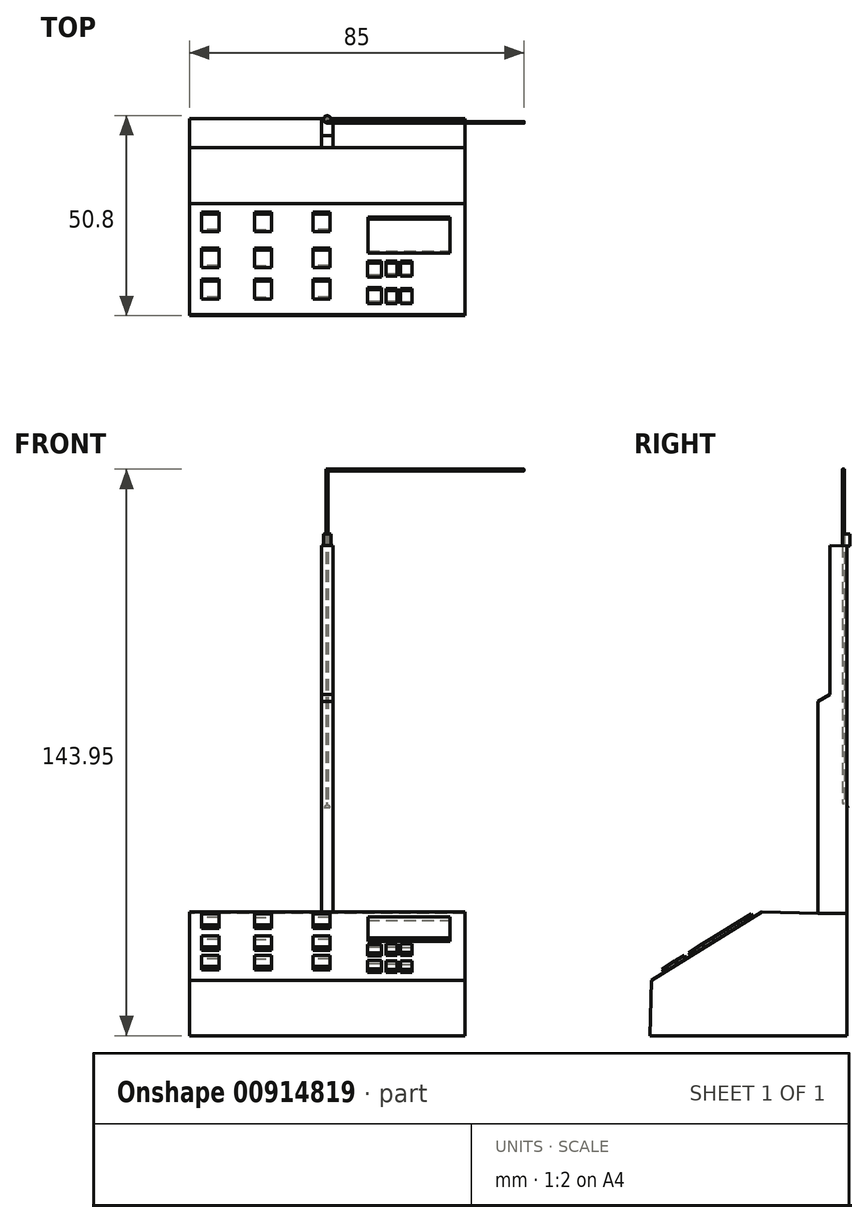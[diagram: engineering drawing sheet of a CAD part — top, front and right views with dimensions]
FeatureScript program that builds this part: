
annotation { "Feature Type Name" : "Feature", "Feature Type Description" : "" }
export const myFeature = defineFeature(function(context is Context, id is Id, definition is map)
    precondition{}
    {
        {
            var Q0;
            Q0=qCreatedBy(makeId("Right.planeOp"),FACE);
            var sketch = newSketch(context, id + "F0", { "sketchPlane" : qUnion([Q0])});
            skLineSegment(sketch, "E0", {"start": v(0, 124.44) * mm, "end": v(0, 0) * mm});
            skLineSegment(sketch, "E1", {"start": v(0, 0) * mm, "end": v(-50, 0) * mm});
            skLineSegment(sketch, "E2", {"start": v(-50, 0) * mm, "end": v(-49.7, 14.02) * mm});
            skLineSegment(sketch, "E3", {"start": v(-49.7, 14.02) * mm, "end": v(-21.55, 31.4) * mm});
            skLineSegment(sketch, "E4", {"start": v(-21.55, 31.4) * mm, "end": v(-7.35, 31.1) * mm});
            skLineSegment(sketch, "E5", {"start": v(-7.35, 31.1) * mm, "end": v(-7.35, 84.93) * mm});
            skLineSegment(sketch, "E6", {"start": v(-7.35, 84.93) * mm, "end": v(-4.25, 86.74) * mm});
            skLineSegment(sketch, "E7", {"start": v(-4.25, 86.74) * mm, "end": v(-4.25, 124.49) * mm});
            skLineSegment(sketch, "E8", {"start": v(-4.25, 124.49) * mm, "end": v(0, 124.44) * mm});
            skLineSegment(sketch, "E9", {"start": v(-7.35, 31.1) * mm, "end": v(0, 31.1) * mm});
            skSolve(sketch);
        }
        {
            var Q0;
            {var subQ0=sQuery(id+"F0.wireOp",EDGE,"E1");Q0=makeQuery(id+"F0.imprint","IMPRINT",FACE,{"disambiguationData":[TD([[makeQuery(id+"F0.imprint","IMPRINT",EDGE,{"derivedFrom":subQ0}),-1.0]])]});}
            extrude(context, id + "F1", {"entities" : qUnion([Q0]), "endBound" : BoundingType.SYMMETRIC, "depth" : 70 * mm, "offsetDistance" : 25 * mm});
        }
        {
            var Q0;
            Q0 = qSketchRegion(id + "F0", true);
            extrude(context, id + "F2", {"entities" : qUnion([Q0]), "operationType" : NewBodyOperationType.ADD, "endBound" : BoundingType.SYMMETRIC, "depth" : 3 * mm, "offsetDistance" : 25 * mm});
        }
        {
            var Q0;
            Q0=makeQuery(id+"F2.opExtrude","SWEPT_FACE",FACE,{"disambiguationData":[OSD([sQuery(id+"F0.wireOp",EDGE,"E8")])]});
            var sketch = newSketch(context, id + "F3", { "sketchPlane" : qUnion([Q0])});
            skCircle(sketch, "E10", {"center": v(0, -1.6) * mm, "radius": 0.9 * mm});
            skSolve(sketch);
        }
        {
            var Q0;
            Q0 = qSketchRegion(id + "F3", true);
            extrude(context, id + "F4", {"entities" : qUnion([Q0]), "operationType" : NewBodyOperationType.ADD, "depth" : 3 * mm, "offsetDistance" : 25 * mm});
        }
        {
            var Q0;
            Q0=qCreatedBy(makeId("Front.planeOp"),FACE);
            cPlane(context, id + "F5", {"entities" : qUnion([Q0]), "cplaneType" : CPlaneType.OFFSET, "offset" : 0.9 * mm, "width" : 150 * mm, "height" : 150 * mm});
        }
        {
            var Q0;
            Q0=qCreatedBy(id+"F5.planeOp",FACE);
            var sketch = newSketch(context, id + "F6", { "sketchPlane" : qUnion([Q0])});
            skLineSegment(sketch, "E11", {"start": v(0, 57.63) * mm, "end": v(0, 58.95) * mm});
            skArc(sketch, "E12", {"start": v(0, 58.95) * mm, "mid": v(-0.77, 58.67) * mm, "end": v(-1.18, 57.97) * mm});
            skLineSegment(sketch, "E13", {"start": v(-0.9, 57.97) * mm, "end": v(-1.18, 57.97) * mm});
            skLineSegment(sketch, "E14", {"start": v(-1.18, 57.97) * mm, "end": v(0, 57.97) * mm});
            skSolve(sketch);
        }
        {
            var Q0;
            Q0 = qSketchRegion(id + "F6", true);
            var Q1;
            Q1=sQuery(id+"F6.wireOp",EDGE,"E11");
            revolve(context, id + "F7", {"operationType" : NewBodyOperationType.ADD, "surfaceOperationType" : NewSurfaceOperationType.NEW, "entities" : qUnion([Q0]), "axis" : qUnion([Q1]), "revolveType" : RevolveType.FULL});
        }
        {
            var Q0;
            Q0=qCreatedBy(makeId("Top.planeOp"),FACE);
            cPlane(context, id + "F8", {"entities" : qUnion([Q0]), "cplaneType" : CPlaneType.OFFSET, "offset" : 58.95 * mm, "width" : 150 * mm, "height" : 150 * mm});
        }
        {
            var Q0;
            Q0=qCreatedBy(id+"F8.planeOp",FACE);
            var sketch = newSketch(context, id + "F9", { "sketchPlane" : qUnion([Q0])});
            skCircle(sketch, "E15", {"center": v(0, -0.9) * mm, "radius": 0.25 * mm});
            skSolve(sketch);
        }
        {
            var Q0;
            Q0 = qSketchRegion(id + "F9", true);
            extrude(context, id + "F10", {"entities" : qUnion([Q0]), "depth" : 85 * mm, "offsetDistance" : 25 * mm});
        }
        {
            var Q0;
            Q0=qCreatedBy(makeId("Right.planeOp"),FACE);
            var sketch = newSketch(context, id + "F11", { "sketchPlane" : qUnion([Q0])});
            skCircle(sketch, "E16", {"center": v(-0.9, 143.72) * mm, "radius": 0.22 * mm});
            skSolve(sketch);
        }
        {
            var Q0;
            Q0 = qSketchRegion(id + "F11", true);
            extrude(context, id + "F12", {"entities" : qUnion([Q0]), "operationType" : NewBodyOperationType.ADD, "depth" : 50 * mm, "offsetDistance" : 25 * mm});
        }
        {
            var Q0;
            Q0=makeQuery(id+"F1.opExtrude","SWEPT_FACE",FACE,{"disambiguationData":[OSD([sQuery(id+"F0.wireOp",EDGE,"E3")])]});
            var sketch = newSketch(context, id + "F13", { "sketchPlane" : qUnion([Q0])});
            skLineSegment(sketch, "E17.bottom", {"start": v(-27.54, -9.63) * mm, "end": v(-31.88, -9.63) * mm});
            skLineSegment(sketch, "E17.top", {"start": v(-27.54, -4.3) * mm, "end": v(-31.88, -4.3) * mm});
            skLineSegment(sketch, "E17.left", {"start": v(-27.54, -9.63) * mm, "end": v(-27.54, -4.3) * mm});
            skLineSegment(sketch, "E17.right", {"start": v(-31.88, -9.63) * mm, "end": v(-31.88, -4.3) * mm});
            skPoint(sketch, "E17.middle", {"position": v(-29.71, -6.96) * mm});
            skLineSegment(sketch, "E18", {"start": v(-23.03, -3.38) * mm, "end": v(-23.03, -27.56) * mm});
            skLineSegment(sketch, "E19", {"start": v(-8.92, -3.02) * mm, "end": v(-8.92, -27.82) * mm});
            skLineSegment(sketch, "E20", {"start": v(-32.63, -22.37) * mm, "end": v(1.6, -22.37) * mm});
            skLineSegment(sketch, "E21.MirrorCS", {"start": v(-18.52, -4.3) * mm, "end": v(-14.18, -4.3) * mm});
            skLineSegment(sketch, "E22.MirrorCS", {"start": v(-18.52, -9.63) * mm, "end": v(-18.52, -4.3) * mm});
            skLineSegment(sketch, "E23.MirrorCS", {"start": v(-18.52, -9.63) * mm, "end": v(-14.18, -9.63) * mm});
            skLineSegment(sketch, "E24.MirrorCS", {"start": v(-14.18, -9.63) * mm, "end": v(-14.18, -4.3) * mm});
            skLineSegment(sketch, "E25.MirrorCS", {"start": v(-27.54, -15.05) * mm, "end": v(-27.54, -20.37) * mm});
            skLineSegment(sketch, "E26.MirrorCS", {"start": v(-27.54, -20.37) * mm, "end": v(-31.88, -20.37) * mm});
            skLineSegment(sketch, "E27.MirrorCS", {"start": v(-31.88, -15.05) * mm, "end": v(-31.88, -20.37) * mm});
            skLineSegment(sketch, "E28.MirrorCS", {"start": v(-27.54, -15.05) * mm, "end": v(-31.88, -15.05) * mm});
            skLineSegment(sketch, "E29.MirrorCS", {"start": v(-18.52, -15.05) * mm, "end": v(-14.18, -15.05) * mm});
            skLineSegment(sketch, "E30.MirrorCS", {"start": v(-18.52, -15.05) * mm, "end": v(-18.52, -20.37) * mm});
            skLineSegment(sketch, "E31.MirrorCS", {"start": v(-18.52, -20.37) * mm, "end": v(-14.18, -20.37) * mm});
            skLineSegment(sketch, "E32.MirrorCS", {"start": v(-14.18, -15.05) * mm, "end": v(-14.18, -20.37) * mm});
            skLineSegment(sketch, "E33.MirrorCS", {"start": v(-3.67, -9.63) * mm, "end": v(-3.67, -4.3) * mm});
            skLineSegment(sketch, "E34.MirrorCS", {"start": v(0.68, -9.63) * mm, "end": v(-3.67, -9.63) * mm});
            skLineSegment(sketch, "E35.MirrorCS", {"start": v(0.68, -9.63) * mm, "end": v(0.68, -4.3) * mm});
            skLineSegment(sketch, "E36.MirrorCS", {"start": v(0.68, -4.3) * mm, "end": v(-3.67, -4.3) * mm});
            skLineSegment(sketch, "E37.MirrorCS", {"start": v(0.68, -15.05) * mm, "end": v(-3.67, -15.05) * mm});
            skLineSegment(sketch, "E38.MirrorCS", {"start": v(0.68, -15.05) * mm, "end": v(0.68, -20.37) * mm});
            skLineSegment(sketch, "E39.MirrorCS", {"start": v(0.68, -20.37) * mm, "end": v(-3.67, -20.37) * mm});
            skLineSegment(sketch, "E40.MirrorCS", {"start": v(-3.67, -15.05) * mm, "end": v(-3.67, -20.37) * mm});
            skLineSegment(sketch, "E41.MirrorCS", {"start": v(-27.54, -24.36) * mm, "end": v(-31.88, -24.36) * mm});
            skLineSegment(sketch, "E42.MirrorCS", {"start": v(-31.88, -29.68) * mm, "end": v(-31.88, -24.36) * mm});
            skLineSegment(sketch, "E43.MirrorCS", {"start": v(-27.54, -29.68) * mm, "end": v(-31.88, -29.68) * mm});
            skLineSegment(sketch, "E44.MirrorCS", {"start": v(-27.54, -29.68) * mm, "end": v(-27.54, -24.36) * mm});
            skLineSegment(sketch, "E45.MirrorCS", {"start": v(-18.52, -29.68) * mm, "end": v(-18.52, -24.36) * mm});
            skLineSegment(sketch, "E46.MirrorCS", {"start": v(-18.52, -29.68) * mm, "end": v(-14.18, -29.68) * mm});
            skLineSegment(sketch, "E47.MirrorCS", {"start": v(-14.18, -29.68) * mm, "end": v(-14.18, -24.36) * mm});
            skLineSegment(sketch, "E48.MirrorCS", {"start": v(-18.52, -24.36) * mm, "end": v(-14.18, -24.36) * mm});
            skLineSegment(sketch, "E49.MirrorCS", {"start": v(0.68, -24.36) * mm, "end": v(-3.67, -24.36) * mm});
            skLineSegment(sketch, "E50.MirrorCS", {"start": v(-3.67, -29.68) * mm, "end": v(-3.67, -24.36) * mm});
            skLineSegment(sketch, "E51.MirrorCS", {"start": v(0.68, -29.68) * mm, "end": v(-3.67, -29.68) * mm});
            skLineSegment(sketch, "E52.MirrorCS", {"start": v(0.68, -29.68) * mm, "end": v(0.68, -24.36) * mm});
            skLineSegment(sketch, "E53.bottom", {"start": v(10.3, -5.9) * mm, "end": v(31.24, -5.9) * mm});
            skLineSegment(sketch, "E53.top", {"start": v(10.3, -16) * mm, "end": v(31.24, -16) * mm});
            skLineSegment(sketch, "E53.left", {"start": v(10.3, -5.9) * mm, "end": v(10.3, -16) * mm});
            skLineSegment(sketch, "E53.right", {"start": v(31.24, -5.9) * mm, "end": v(31.24, -16) * mm});
            skPoint(sketch, "E53.middle", {"position": v(20.77, -10.95) * mm});
            skLineSegment(sketch, "E54.bottom", {"start": v(13.74, -23.1) * mm, "end": v(10.18, -23.1) * mm});
            skLineSegment(sketch, "E54.top", {"start": v(13.74, -19) * mm, "end": v(10.18, -19) * mm});
            skLineSegment(sketch, "E54.left", {"start": v(13.74, -23.1) * mm, "end": v(13.74, -19) * mm});
            skLineSegment(sketch, "E54.right", {"start": v(10.18, -23.1) * mm, "end": v(10.18, -19) * mm});
            skPoint(sketch, "E54.middle", {"position": v(11.96, -21.05) * mm});
            skLineSegment(sketch, "E55.bottom", {"start": v(17.7, -22.87) * mm, "end": v(14.95, -22.87) * mm});
            skLineSegment(sketch, "E55.top", {"start": v(17.7, -18.95) * mm, "end": v(14.95, -18.95) * mm});
            skLineSegment(sketch, "E55.left", {"start": v(17.7, -22.87) * mm, "end": v(17.7, -18.95) * mm});
            skLineSegment(sketch, "E55.right", {"start": v(14.95, -22.87) * mm, "end": v(14.95, -18.95) * mm});
            skPoint(sketch, "E55.middle", {"position": v(16.33, -20.91) * mm});
            skLineSegment(sketch, "E56.bottom", {"start": v(18.63, -18.95) * mm, "end": v(21.59, -18.95) * mm});
            skLineSegment(sketch, "E56.top", {"start": v(18.63, -22.85) * mm, "end": v(21.59, -22.85) * mm});
            skLineSegment(sketch, "E56.left", {"start": v(18.63, -18.95) * mm, "end": v(18.63, -22.85) * mm});
            skLineSegment(sketch, "E56.right", {"start": v(21.59, -18.95) * mm, "end": v(21.59, -22.85) * mm});
            skPoint(sketch, "E56.middle", {"position": v(20.1, -20.9) * mm});
            skLineSegment(sketch, "E57", {"start": v(10.18, -25) * mm, "end": v(27.28, -25) * mm});
            skLineSegment(sketch, "E58.MirrorCS", {"start": v(18.63, -27.16) * mm, "end": v(21.59, -27.16) * mm});
            skLineSegment(sketch, "E59.MirrorCS", {"start": v(18.63, -31.05) * mm, "end": v(18.63, -27.16) * mm});
            skLineSegment(sketch, "E60.MirrorCS", {"start": v(18.63, -31.05) * mm, "end": v(21.59, -31.05) * mm});
            skLineSegment(sketch, "E61.MirrorCS", {"start": v(21.59, -31.05) * mm, "end": v(21.59, -27.16) * mm});
            skLineSegment(sketch, "E62.MirrorCS", {"start": v(17.7, -27.13) * mm, "end": v(17.7, -31.05) * mm});
            skLineSegment(sketch, "E63.MirrorCS", {"start": v(17.7, -31.05) * mm, "end": v(14.95, -31.05) * mm});
            skLineSegment(sketch, "E64.MirrorCS", {"start": v(14.95, -27.13) * mm, "end": v(14.95, -31.05) * mm});
            skLineSegment(sketch, "E65.MirrorCS", {"start": v(17.7, -27.13) * mm, "end": v(14.95, -27.13) * mm});
            skLineSegment(sketch, "E66.MirrorCS", {"start": v(13.74, -26.9) * mm, "end": v(10.18, -26.9) * mm});
            skLineSegment(sketch, "E67.MirrorCS", {"start": v(10.18, -26.9) * mm, "end": v(10.18, -31) * mm});
            skLineSegment(sketch, "E68.MirrorCS", {"start": v(13.74, -31) * mm, "end": v(10.18, -31) * mm});
            skLineSegment(sketch, "E69.MirrorCS", {"start": v(13.74, -26.9) * mm, "end": v(13.74, -31) * mm});
            skSolve(sketch);
        }
        {
            var Q0;
            Q0 = qSketchRegion(id + "F13", true);
            extrude(context, id + "F14", {"entities" : qUnion([Q0]), "operationType" : NewBodyOperationType.ADD, "depth" : 1 * mm, "offsetDistance" : 25 * mm});
        }
    });
